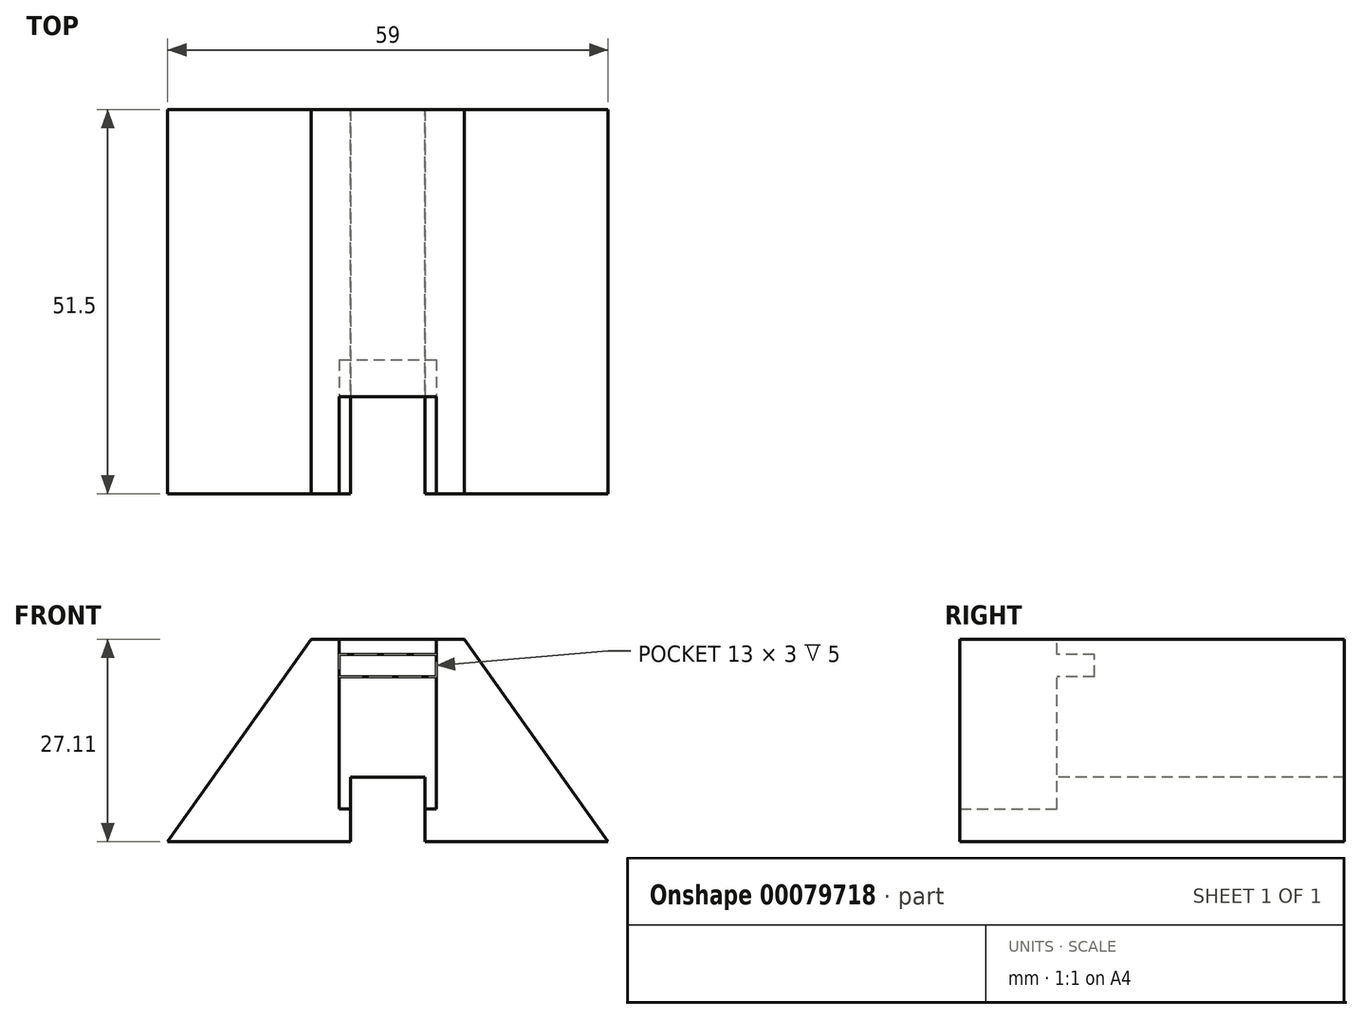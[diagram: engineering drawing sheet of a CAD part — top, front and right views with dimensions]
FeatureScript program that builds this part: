
annotation { "Feature Type Name" : "Feature", "Feature Type Description" : "" }
export const myFeature = defineFeature(function(context is Context, id is Id, definition is map)
    precondition{}
    {
        {
            var Q0;
            Q0=qCreatedBy(makeId("Top.planeOp"),FACE);
            var sketch = newSketch(context, id + "F0", { "sketchPlane" : qUnion([Q0])});
            skLineSegment(sketch, "E0.bottom", {"start": v(29.5, 25.75) * mm, "end": v(-29.5, 25.75) * mm});
            skLineSegment(sketch, "E0.top", {"start": v(29.5, -25.75) * mm, "end": v(-29.5, -25.75) * mm});
            skLineSegment(sketch, "E0.left", {"start": v(29.5, 25.75) * mm, "end": v(29.5, -25.75) * mm});
            skLineSegment(sketch, "E0.right", {"start": v(-29.5, 25.75) * mm, "end": v(-29.5, -25.75) * mm});
            skPoint(sketch, "E0.middle", {"position": v(0, 0) * mm});
            skSolve(sketch);
        }
        {
            var Q0;
            Q0=makeQuery(id+"F0.imprint","IMPRINT",FACE,{"disambiguationData":[TD([[makeQuery(id+"F0.imprint","IMPRINT",EDGE,{"derivedFrom":sQuery(id+"F0.wireOp",EDGE,"E0.bottom")}),1.0]])]});
            var sketch = newSketch(context, id + "F1", { "sketchPlane" : qUnion([Q0])});
            skLineSegment(sketch, "E1.bottom", {"start": v(10.25, -25.75) * mm, "end": v(-10.25, -25.75) * mm});
            skLineSegment(sketch, "E1.top", {"start": v(10.25, 25.75) * mm, "end": v(-10.25, 25.75) * mm});
            skLineSegment(sketch, "E1.left", {"start": v(10.25, -25.75) * mm, "end": v(10.25, 25.75) * mm});
            skLineSegment(sketch, "E1.right", {"start": v(-10.25, -25.75) * mm, "end": v(-10.25, 25.75) * mm});
            skPoint(sketch, "E1.middle", {"position": v(0, 0) * mm});
            skSolve(sketch);
        }
        {
            var Q0;
            Q0 = qSketchRegion(id + "F1", true);
            extrude(context, id + "F2", {"entities" : qUnion([Q0]), "depth" : 27.1 * mm});
        }
        {
            var Q0;
            Q0=makeQuery(id+"F2.opExtrude","CAP_FACE",FACE,{"disambiguationData":[OSD([sQuery(id+"F1.wireOp",EDGE,"E1.bottom"),sQuery(id+"F1.wireOp",EDGE,"E1.top"),sQuery(id+"F1.wireOp",EDGE,"E1.left"),sQuery(id+"F1.wireOp",EDGE,"E1.right")])],"isStart":false});
            var sketch = newSketch(context, id + "F3", { "sketchPlane" : qUnion([Q0])});
            skLineSegment(sketch, "E2.bottom", {"start": v(10.25, 25.75) * mm, "end": v(-10.25, 25.75) * mm});
            skLineSegment(sketch, "E2.top", {"start": v(10.25, -25.75) * mm, "end": v(-10.25, -25.75) * mm});
            skLineSegment(sketch, "E2.left", {"start": v(10.25, 25.75) * mm, "end": v(10.25, -25.75) * mm});
            skLineSegment(sketch, "E2.right", {"start": v(-10.25, 25.75) * mm, "end": v(-10.25, -25.75) * mm});
            skPoint(sketch, "E2.middle", {"position": v(0, 0) * mm});
            skSolve(sketch);
        }
        {
            var Q0;
            Q0=makeQuery(id+"F0.imprint","IMPRINT",FACE,{"disambiguationData":[TD([[makeQuery(id+"F0.imprint","IMPRINT",EDGE,{"derivedFrom":sQuery(id+"F0.wireOp",EDGE,"E0.bottom")}),1.0]])]});
            var sketch = newSketch(context, id + "F4", { "sketchPlane" : qUnion([Q0])});
            skLineSegment(sketch, "E3.bottom", {"start": v(-29.5, 25.75) * mm, "end": v(29.5, 25.75) * mm});
            skLineSegment(sketch, "E3.top", {"start": v(-29.5, -25.75) * mm, "end": v(29.5, -25.75) * mm});
            skLineSegment(sketch, "E3.left", {"start": v(-29.5, 25.75) * mm, "end": v(-29.5, -25.75) * mm});
            skLineSegment(sketch, "E3.right", {"start": v(29.5, 25.75) * mm, "end": v(29.5, -25.75) * mm});
            skPoint(sketch, "E3.middle", {"position": v(0, 0) * mm});
            skSolve(sketch);
        }
        {
            var Q1;
            Q1=makeQuery(id+"F4.imprint","IMPRINT",FACE,{"disambiguationData":[TD([[makeQuery(id+"F4.imprint","IMPRINT",EDGE,{"derivedFrom":sQuery(id+"F4.wireOp",EDGE,"E3.bottom")}),1.0]])]});
            var Q2;
            Q2=makeQuery(id+"F3.imprint","IMPRINT",FACE,{"disambiguationData":[TD([[makeQuery(id+"F3.imprint","IMPRINT",EDGE,{"derivedFrom":sQuery(id+"F3.wireOp",EDGE,"E2.bottom")}),1.0]])]});
            loft(context, id + "F5", {"operationType" : NewBodyOperationType.ADD, "sheetProfilesArray" : [{ "sheetProfileEntities" : qUnion([Q1]) }, { "sheetProfileEntities" : qUnion([Q2]) }]});
        }
        {
            var Q0;
            Q0=makeQuery(id+"F2.opExtrude","CAP_FACE",FACE,{"disambiguationData":[OSD([sQuery(id+"F1.wireOp",EDGE,"E1.bottom"),sQuery(id+"F1.wireOp",EDGE,"E1.top"),sQuery(id+"F1.wireOp",EDGE,"E1.left"),sQuery(id+"F1.wireOp",EDGE,"E1.right")])],"isStart":false});
            var sketch = newSketch(context, id + "F6", { "sketchPlane" : qUnion([Q0])});
            skLineSegment(sketch, "E4.bottom", {"start": v(5, -12.75) * mm, "end": v(-5, -12.75) * mm});
            skLineSegment(sketch, "E4.top", {"start": v(5, -25.75) * mm, "end": v(-5, -25.75) * mm});
            skLineSegment(sketch, "E4.left", {"start": v(5, -12.75) * mm, "end": v(5, -25.75) * mm});
            skLineSegment(sketch, "E4.right", {"start": v(-5, -12.75) * mm, "end": v(-5, -25.75) * mm});
            skPoint(sketch, "E4.middle", {"position": v(0, -19.25) * mm});
            skLineSegment(sketch, "E5", {"start": v(0, 0) * mm, "end": v(0, -48.85) * mm, "construction": true});
            skPoint(sketch, "E5.endSnap0", {"position": v(0, -25.75) * mm});
            skSolve(sketch);
        }
        {
            var Q0;
            Q0 = qSketchRegion(id + "F6", true);
            var Q1;
            Q1=makeQuery(id+"F5.boolean.opBoolean","MERGE",FACE,{"derivedFrom":[makeQuery(id+"F2.opExtrude","CAP_FACE",FACE,{"disambiguationData":[OSD([sQuery(id+"F1.wireOp",EDGE,"E1.bottom"),sQuery(id+"F1.wireOp",EDGE,"E1.top"),sQuery(id+"F1.wireOp",EDGE,"E1.left"),sQuery(id+"F1.wireOp",EDGE,"E1.right")])],"isStart":true}),makeQuery(id+"F5.opLoft","CAP_FACE",FACE,{"disambiguationData":[OSD([makeQuery(id+"F4.imprint","IMPRINT",FACE,{"disambiguationData":[TD([[makeQuery(id+"F4.imprint","IMPRINT",EDGE,{"derivedFrom":sQuery(id+"F4.wireOp",EDGE,"E3.bottom")}),1.0]])]})])],"isStart":true})]});
            extrude(context, id + "F7", {"entities" : qUnion([Q0]), "operationType" : NewBodyOperationType.REMOVE, "endBound" : BoundingType.UP_TO_SURFACE, "oppositeDirection" : true, "endBoundEntityFace" : qUnion([Q1]), "depth" : 25 * mm});
        }
        {
            var Q0;
            Q0=makeQuery(id+"F2.opExtrude","CAP_FACE",FACE,{"disambiguationData":[OSD([sQuery(id+"F1.wireOp",EDGE,"E1.bottom"),sQuery(id+"F1.wireOp",EDGE,"E1.top"),sQuery(id+"F1.wireOp",EDGE,"E1.left"),sQuery(id+"F1.wireOp",EDGE,"E1.right")])],"isStart":false});
            var sketch = newSketch(context, id + "F8", { "sketchPlane" : qUnion([Q0])});
            skLineSegment(sketch, "E6.bottom", {"start": v(-6.5, -12.75) * mm, "end": v(6.5, -12.75) * mm});
            skLineSegment(sketch, "E6.top", {"start": v(-6.5, -25.75) * mm, "end": v(6.5, -25.75) * mm});
            skLineSegment(sketch, "E6.left", {"start": v(-6.5, -12.75) * mm, "end": v(-6.5, -25.75) * mm});
            skLineSegment(sketch, "E6.right", {"start": v(6.5, -12.75) * mm, "end": v(6.5, -25.75) * mm});
            skSolve(sketch);
        }
        {
            var Q0;
            Q0 = qSketchRegion(id + "F8", true);
            extrude(context, id + "F9", {"entities" : qUnion([Q0]), "operationType" : NewBodyOperationType.REMOVE, "oppositeDirection" : true, "depth" : 22.75 * mm});
        }
        {
            var Q0;
            Q0=makeQuery(id+"F9.boolean.opBoolean","MERGE",FACE,{"derivedFrom":[makeQuery(id+"F7.boolean.opBoolean","COPY",FACE,{"derivedFrom":makeQuery(id+"F7.opExtrude","SWEPT_FACE",FACE,{"disambiguationData":[OSD([sQuery(id+"F6.wireOp",EDGE,"E4.bottom")])]})})],"fromTools":[makeQuery(id+"F9.opExtrude","SWEPT_FACE",FACE,{"disambiguationData":[OSD([sQuery(id+"F8.wireOp",EDGE,"E6.bottom")])]})]});
            var sketch = newSketch(context, id + "F10", { "sketchPlane" : qUnion([Q0])});
            skLineSegment(sketch, "E7.bottom", {"start": v(5, 0) * mm, "end": v(-5, 0) * mm});
            skLineSegment(sketch, "E7.top", {"start": v(5, 8.67) * mm, "end": v(-5, 8.67) * mm});
            skLineSegment(sketch, "E7.left", {"start": v(5, 0) * mm, "end": v(5, 8.67) * mm});
            skLineSegment(sketch, "E7.right", {"start": v(-5, 0) * mm, "end": v(-5, 8.67) * mm});
            skSolve(sketch);
        }
        {
            var Q0;
            Q0 = qSketchRegion(id + "F10", true);
            var Q1;
            Q1=makeQuery(id+"F5.boolean.opBoolean","MERGE",FACE,{"derivedFrom":[makeQuery(id+"F2.opExtrude","SWEPT_FACE",FACE,{"disambiguationData":[OSD([sQuery(id+"F1.wireOp",EDGE,"E1.top")])]}),makeQuery(id+"F5.opLoft","SWEPT_FACE",FACE,{"disambiguationData":[OSD([sQuery(id+"F3.wireOp",EDGE,"E2.bottom"),sQuery(id+"F3.wireOp",EDGE,"E2.left"),sQuery(id+"F3.wireOp",EDGE,"E2.right"),sQuery(id+"F4.wireOp",EDGE,"E3.bottom"),sQuery(id+"F4.wireOp",EDGE,"E3.left"),sQuery(id+"F4.wireOp",EDGE,"E3.right")])]})]});
            extrude(context, id + "F11", {"entities" : qUnion([Q0]), "operationType" : NewBodyOperationType.REMOVE, "endBound" : BoundingType.UP_TO_SURFACE, "oppositeDirection" : true, "endBoundEntityFace" : qUnion([Q1]), "depth" : 25 * mm});
        }
        {
            var Q0;
            Q0=makeQuery(id+"F9.boolean.opBoolean","MERGE",FACE,{"derivedFrom":[makeQuery(id+"F7.boolean.opBoolean","COPY",FACE,{"derivedFrom":makeQuery(id+"F7.opExtrude","SWEPT_FACE",FACE,{"disambiguationData":[OSD([sQuery(id+"F6.wireOp",EDGE,"E4.bottom")])]})})],"fromTools":[makeQuery(id+"F9.opExtrude","SWEPT_FACE",FACE,{"disambiguationData":[OSD([sQuery(id+"F8.wireOp",EDGE,"E6.bottom")])]})]});
            var sketch = newSketch(context, id + "F12", { "sketchPlane" : qUnion([Q0])});
            skLineSegment(sketch, "E8.bottom", {"start": v(-6.5, 25.1) * mm, "end": v(6.5, 25.1) * mm});
            skLineSegment(sketch, "E8.top", {"start": v(-6.5, 22.1) * mm, "end": v(6.5, 22.1) * mm});
            skLineSegment(sketch, "E8.left", {"start": v(-6.5, 25.1) * mm, "end": v(-6.5, 22.1) * mm});
            skLineSegment(sketch, "E8.right", {"start": v(6.5, 25.1) * mm, "end": v(6.5, 22.1) * mm});
            skSolve(sketch);
        }
        {
            var Q0;
            Q0 = qSketchRegion(id + "F12", true);
            extrude(context, id + "F13", {"entities" : qUnion([Q0]), "operationType" : NewBodyOperationType.REMOVE, "oppositeDirection" : true, "depth" : 5 * mm});
        }
    });
